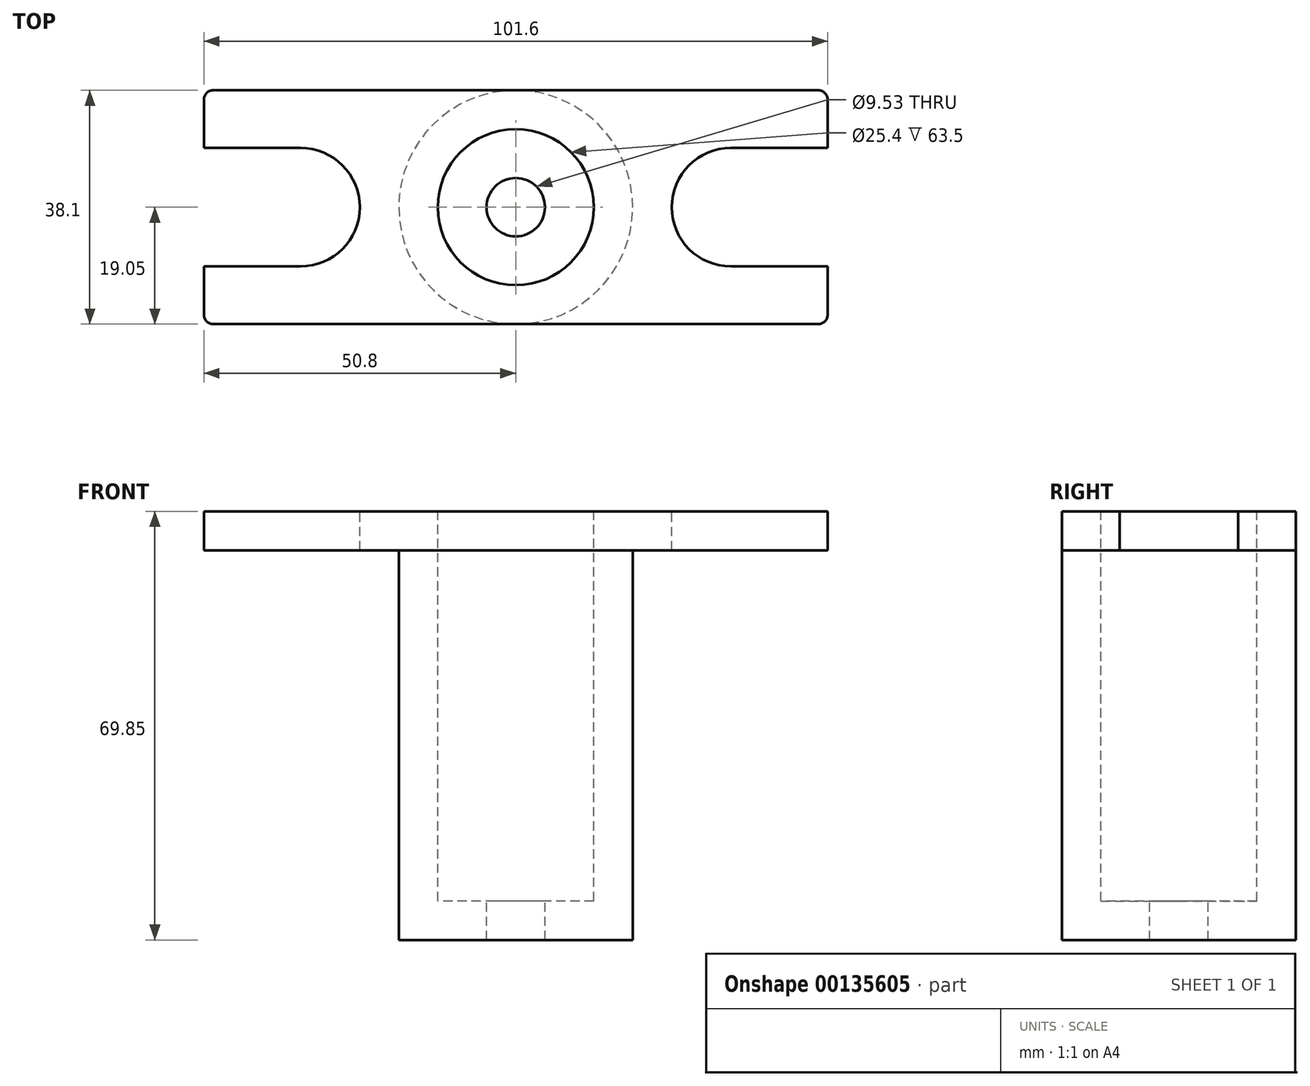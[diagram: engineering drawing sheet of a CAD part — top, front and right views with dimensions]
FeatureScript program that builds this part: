
annotation { "Feature Type Name" : "Feature", "Feature Type Description" : "" }
export const myFeature = defineFeature(function(context is Context, id is Id, definition is map)
    precondition{}
    {
        {
            var Q0;
            Q0=qCreatedBy(makeId("Front.planeOp"),FACE);
            var sketch = newSketch(context, id + "F0", { "sketchPlane" : qUnion([Q0])});
            skLineSegment(sketch, "E0", {"start": v(0, -26.8) * mm, "end": v(0, 86.68) * mm, "construction": true});
            skLineSegment(sketch, "E1", {"start": v(0, 69.85) * mm, "end": v(50.8, 69.85) * mm});
            skLineSegment(sketch, "E2", {"start": v(50.8, 69.85) * mm, "end": v(50.8, 63.5) * mm});
            skLineSegment(sketch, "E3", {"start": v(50.8, 63.5) * mm, "end": v(0, 63.5) * mm});
            skLineSegment(sketch, "E4", {"start": v(19.05, 63.5) * mm, "end": v(19.05, 0) * mm});
            skLineSegment(sketch, "E5", {"start": v(19.05, 0) * mm, "end": v(0, 0) * mm});
            skLineSegment(sketch, "E6", {"start": v(0, 0) * mm, "end": v(0, 69.85) * mm});
            skSolve(sketch);
        }
        {
            var Q0;
            Q0 = qSketchRegion(id + "F0", true);
            var Q1;
            Q1=sQuery(id+"F0.wireOp",EDGE,"E0");
            revolve(context, id + "F1", {"entities" : qUnion([Q0]), "axis" : qUnion([Q1]), "revolveType" : RevolveType.FULL});
        }
        {
            var Q0;
            Q0=makeQuery(id+"F1.opRevolve","SWEPT_FACE",FACE,{"disambiguationData":[OSD([sQuery(id+"F0.wireOp",EDGE,"E1")])]});
            var sketch = newSketch(context, id + "F2", { "sketchPlane" : qUnion([Q0])});
            skLineSegment(sketch, "E7.bottom", {"start": v(-50.8, 19.05) * mm, "end": v(50.8, 19.05) * mm});
            skLineSegment(sketch, "E7.top", {"start": v(-50.8, -19.05) * mm, "end": v(50.8, -19.05) * mm});
            skLineSegment(sketch, "E7.left", {"start": v(-50.8, 19.05) * mm, "end": v(-50.8, -19.05) * mm});
            skLineSegment(sketch, "E7.right", {"start": v(50.8, 19.05) * mm, "end": v(50.8, -19.05) * mm});
            skLineSegment(sketch, "E8", {"start": v(-73.34, 0) * mm, "end": v(77.6, 0) * mm, "construction": true});
            skLineSegment(sketch, "E9", {"start": v(0, -57.62) * mm, "end": v(0, 62.73) * mm, "construction": true});
            skSolve(sketch);
        }
        {
            var Q0;
            {var subQ0=sQuery(id+"F2.wireOp",EDGE,"E7.left");var subQ1=sQuery(id+"F2.wireOp",EDGE,"E7.bottom");var subQ2=makeQuery(id+"F2.imprint","INTERSECT",VERTEX,{"derivedFrom":[subQ1,subQ0]});Q0=makeQuery(id+"F2.imprint","IMPRINT",FACE,{"disambiguationData":[TD([[makeQuery(id+"F2.imprint","IMPRINT",EDGE,{"disambiguationData":[TD([[subQ2,-1.0]])],"derivedFrom":subQ1}),-1.0]])]});}
            var Q1;
            {var subQ0=sQuery(id+"F2.wireOp",EDGE,"E7.right");var subQ1=sQuery(id+"F2.wireOp",EDGE,"E7.bottom");var subQ2=makeQuery(id+"F2.imprint","INTERSECT",VERTEX,{"derivedFrom":[subQ1,subQ0]});Q1=makeQuery(id+"F2.imprint","IMPRINT",FACE,{"disambiguationData":[TD([[makeQuery(id+"F2.imprint","IMPRINT",EDGE,{"disambiguationData":[TD([[subQ2,1.0]])],"derivedFrom":subQ1}),-1.0]])]});}
            var Q2;
            {var subQ0=sQuery(id+"F2.wireOp",EDGE,"E7.left");var subQ1=sQuery(id+"F2.wireOp",EDGE,"E7.top");var subQ2=makeQuery(id+"F2.imprint","INTERSECT",VERTEX,{"derivedFrom":[subQ1,subQ0]});Q2=makeQuery(id+"F2.imprint","IMPRINT",FACE,{"disambiguationData":[TD([[makeQuery(id+"F2.imprint","IMPRINT",EDGE,{"disambiguationData":[TD([[subQ2,-1.0]])],"derivedFrom":subQ1}),1.0]])]});}
            var Q3;
            {var subQ0=sQuery(id+"F2.wireOp",EDGE,"E7.right");var subQ1=sQuery(id+"F2.wireOp",EDGE,"E7.top");var subQ2=makeQuery(id+"F2.imprint","INTERSECT",VERTEX,{"derivedFrom":[subQ1,subQ0]});Q3=makeQuery(id+"F2.imprint","IMPRINT",FACE,{"disambiguationData":[TD([[makeQuery(id+"F2.imprint","IMPRINT",EDGE,{"disambiguationData":[TD([[subQ2,1.0]])],"derivedFrom":subQ1}),1.0]])]});}
            var Q4;
            {var subQ0=sQuery(id+"F2.wireOp",EDGE,"E7.top");var subQ1=makeQuery(id+"F1.opRevolve","SWEPT_EDGE",EDGE,{"disambiguationData":[OSD([sQuery(id+"F0.wireOp",EDGE,"E1"),sQuery(id+"F0.wireOp",EDGE,"E2")])]});var subQ2=makeQuery(id+"F2.imprint","INTERSECT",VERTEX,{"disambiguationData":[OD(0.0)],"derivedFrom":[subQ1,subQ0]});Q4=makeQuery(id+"F2.imprint","IMPRINT",FACE,{"disambiguationData":[TD([[makeQuery(id+"F2.imprint","IMPRINT",EDGE,{"disambiguationData":[TD([[subQ2,-1.0]])],"derivedFrom":subQ0}),-1.0]])]});}
            var Q5;
            {var subQ0=sQuery(id+"F2.wireOp",EDGE,"E7.bottom");var subQ1=makeQuery(id+"F1.opRevolve","SWEPT_EDGE",EDGE,{"disambiguationData":[OSD([sQuery(id+"F0.wireOp",EDGE,"E1"),sQuery(id+"F0.wireOp",EDGE,"E2")])]});var subQ2=makeQuery(id+"F2.imprint","INTERSECT",VERTEX,{"disambiguationData":[OD(0.0)],"derivedFrom":[subQ1,subQ0]});Q5=makeQuery(id+"F2.imprint","IMPRINT",FACE,{"disambiguationData":[TD([[makeQuery(id+"F2.imprint","IMPRINT",EDGE,{"disambiguationData":[TD([[subQ2,-1.0]])],"derivedFrom":subQ0}),1.0]])]});}
            extrude(context, id + "F3", {"entities" : qUnion([Q0, Q1, Q2, Q3, Q4, Q5]), "operationType" : NewBodyOperationType.REMOVE, "endBound" : BoundingType.THROUGH_ALL, "oppositeDirection" : true, "depth" : 25.4 * mm});
        }
        {
            var Q0;
            Q0=makeQuery(id+"F1.opRevolve","SWEPT_FACE",FACE,{"disambiguationData":[OSD([sQuery(id+"F0.wireOp",EDGE,"E1")])]});
            var sketch = newSketch(context, id + "F4", { "sketchPlane" : qUnion([Q0])});
            skLineSegment(sketch, "E10.0.0", {"start": v(-47.1, 19.05) * mm, "end": v(-50.8, 19.05) * mm});
            skLineSegment(sketch, "E10.0.1", {"start": v(-50.8, 19.05) * mm, "end": v(-50.8, 0) * mm});
            skArc(sketch, "E10.0.2", {"start": v(-50.8, 0) * mm, "mid": v(-49.86, 9.7) * mm, "end": v(-47.1, 19.05) * mm});
            skLineSegment(sketch, "E11.0.0", {"start": v(-50.8, 0) * mm, "end": v(-50.8, -19.05) * mm});
            skLineSegment(sketch, "E11.0.1", {"start": v(-50.8, -19.05) * mm, "end": v(-47.1, -19.05) * mm});
            skArc(sketch, "E11.0.2", {"start": v(-47.1, -19.05) * mm, "mid": v(-49.86, -9.7) * mm, "end": v(-50.8, 0) * mm});
            skArc(sketch, "E12.0.0", {"start": v(50.8, 0) * mm, "mid": v(49.86, -9.7) * mm, "end": v(47.1, -19.05) * mm});
            skLineSegment(sketch, "E12.0.1", {"start": v(47.1, -19.05) * mm, "end": v(50.8, -19.05) * mm});
            skLineSegment(sketch, "E12.0.2", {"start": v(50.8, -19.05) * mm, "end": v(50.8, 0) * mm});
            skLineSegment(sketch, "E13.0.0", {"start": v(50.8, 19.05) * mm, "end": v(47.1, 19.05) * mm});
            skArc(sketch, "E13.0.1", {"start": v(47.1, 19.05) * mm, "mid": v(49.86, 9.7) * mm, "end": v(50.8, 0) * mm});
            skLineSegment(sketch, "E13.0.2", {"start": v(50.8, 0) * mm, "end": v(50.8, 19.05) * mm});
            skSolve(sketch);
        }
        {
            var Q0;
            Q0 = qSketchRegion(id + "F4", true);
            var Q1;
            Q1=makeQuery(id+"F3.boolean.opBoolean","SPLIT",FACE,{"disambiguationData":[OD(1.0)],"derivedFrom":makeQuery(id+"F1.opRevolve","SWEPT_FACE",FACE,{"disambiguationData":[OSD([sQuery(id+"F0.wireOp",EDGE,"E3")])]})});
            extrude(context, id + "F5", {"entities" : qUnion([Q0]), "operationType" : NewBodyOperationType.ADD, "endBound" : BoundingType.UP_TO_SURFACE, "oppositeDirection" : true, "endBoundEntityFace" : qUnion([Q1]), "depth" : 25.4 * mm});
        }
        {
            var Q0;
            {var subQ0=sQuery(id+"F2.wireOp",EDGE,"E7.bottom");var subQ1=makeQuery(id+"F1.opRevolve","SWEPT_EDGE",EDGE,{"disambiguationData":[OSD([sQuery(id+"F0.wireOp",EDGE,"E1"),sQuery(id+"F0.wireOp",EDGE,"E2")])]});var subQ4=makeQuery(id+"F2.imprint","INTERSECT",VERTEX,{"disambiguationData":[OD(0.0)],"derivedFrom":[subQ1,subQ0]});Q0=makeQuery(id+"F2.imprint","IMPRINT",FACE,{"disambiguationData":[TD([[makeQuery(id+"F2.imprint","IMPRINT",EDGE,{"disambiguationData":[TD([[subQ4,-1.0]])],"derivedFrom":subQ0}),-1.0]])]});}
            var sketch = newSketch(context, id + "F6", { "sketchPlane" : qUnion([Q0])});
            skLineSegment(sketch, "E14", {"start": v(-50.8, 9.65) * mm, "end": v(-35.05, 9.65) * mm});
            skLineSegment(sketch, "E15", {"start": v(-50.8, -9.65) * mm, "end": v(-35.05, -9.65) * mm});
            skLineSegment(sketch, "E16", {"start": v(50.8, -9.65) * mm, "end": v(35.05, -9.65) * mm});
            skLineSegment(sketch, "E17", {"start": v(50.8, 9.65) * mm, "end": v(35.05, 9.65) * mm});
            skArc(sketch, "E18", {"start": v(35.05, 9.65) * mm, "mid": v(25.4, 0) * mm, "end": v(35.05, -9.65) * mm});
            skArc(sketch, "E19", {"start": v(-35.05, -9.65) * mm, "mid": v(-25.4, 0) * mm, "end": v(-35.05, 9.65) * mm});
            skCircle(sketch, "E20", {"center": v(0, 0) * mm, "radius": 12.7 * mm, "construction": true});
            skLineSegment(sketch, "E21", {"start": v(-50.8, -9.65) * mm, "end": v(-50.8, 9.65) * mm});
            skLineSegment(sketch, "E22", {"start": v(50.8, -9.65) * mm, "end": v(50.8, 9.65) * mm});
            skSolve(sketch);
        }
        {
            var Q0;
            {var subQ0=sQuery(id+"F6.wireOp",EDGE,"E19");Q0=makeQuery(id+"F6.imprint","IMPRINT",FACE,{"disambiguationData":[TD([[makeQuery(id+"F6.imprint","IMPRINT",EDGE,{"derivedFrom":subQ0}),1.0]])]});}
            var Q1;
            {var subQ0=sQuery(id+"F6.wireOp",EDGE,"E21");var subQ1=sQuery(id+"F6.wireOp",EDGE,"E14");var subQ2=makeQuery(id+"F6.imprint","INTERSECT",VERTEX,{"derivedFrom":[subQ1,subQ0]});Q1=makeQuery(id+"F6.imprint","IMPRINT",FACE,{"disambiguationData":[TD([[makeQuery(id+"F6.imprint","IMPRINT",EDGE,{"disambiguationData":[TD([[subQ2,-1.0]])],"derivedFrom":subQ1}),-1.0]])]});}
            var Q2;
            {var subQ0=sQuery(id+"F6.wireOp",EDGE,"E21");var subQ1=sQuery(id+"F6.wireOp",EDGE,"E15");var subQ2=makeQuery(id+"F6.imprint","INTERSECT",VERTEX,{"derivedFrom":[subQ1,subQ0]});Q2=makeQuery(id+"F6.imprint","IMPRINT",FACE,{"disambiguationData":[TD([[makeQuery(id+"F6.imprint","IMPRINT",EDGE,{"disambiguationData":[TD([[subQ2,-1.0]])],"derivedFrom":subQ1}),1.0]])]});}
            var Q3;
            {var subQ0=sQuery(id+"F6.wireOp",EDGE,"E18");Q3=makeQuery(id+"F6.imprint","IMPRINT",FACE,{"disambiguationData":[TD([[makeQuery(id+"F6.imprint","IMPRINT",EDGE,{"derivedFrom":subQ0}),1.0]])]});}
            var Q4;
            {var subQ0=sQuery(id+"F6.wireOp",EDGE,"E22");var subQ1=sQuery(id+"F6.wireOp",EDGE,"E17");var subQ2=makeQuery(id+"F6.imprint","INTERSECT",VERTEX,{"derivedFrom":[subQ1,subQ0]});Q4=makeQuery(id+"F6.imprint","IMPRINT",FACE,{"disambiguationData":[TD([[makeQuery(id+"F6.imprint","IMPRINT",EDGE,{"disambiguationData":[TD([[subQ2,-1.0]])],"derivedFrom":subQ1}),1.0]])]});}
            var Q5;
            {var subQ0=sQuery(id+"F6.wireOp",EDGE,"E22");var subQ1=sQuery(id+"F6.wireOp",EDGE,"E16");var subQ2=makeQuery(id+"F6.imprint","INTERSECT",VERTEX,{"derivedFrom":[subQ1,subQ0]});Q5=makeQuery(id+"F6.imprint","IMPRINT",FACE,{"disambiguationData":[TD([[makeQuery(id+"F6.imprint","IMPRINT",EDGE,{"disambiguationData":[TD([[subQ2,-1.0]])],"derivedFrom":subQ1}),-1.0]])]});}
            extrude(context, id + "F7", {"entities" : qUnion([Q0, Q1, Q2, Q3, Q4, Q5]), "operationType" : NewBodyOperationType.REMOVE, "endBound" : BoundingType.THROUGH_ALL, "oppositeDirection" : true, "depth" : 25.4 * mm});
        }
        {
            var Q0;
            Q0=makeQuery(id+"F5.boolean.opBoolean","MERGE",FACE,{"derivedFrom":[makeQuery(id+"F1.opRevolve","SWEPT_FACE",FACE,{"disambiguationData":[OSD([sQuery(id+"F0.wireOp",EDGE,"E1")])]}),makeQuery(id+"F5.opExtrude","CAP_FACE",FACE,{"disambiguationData":[OSD([sQuery(id+"F4.wireOp",EDGE,"E10.0.0"),sQuery(id+"F4.wireOp",EDGE,"E10.0.1"),sQuery(id+"F4.wireOp",EDGE,"E10.0.2")])],"isStart":true}),makeQuery(id+"F5.opExtrude","CAP_FACE",FACE,{"disambiguationData":[OSD([sQuery(id+"F4.wireOp",EDGE,"E11.0.0"),sQuery(id+"F4.wireOp",EDGE,"E11.0.1"),sQuery(id+"F4.wireOp",EDGE,"E11.0.2")])],"isStart":true}),makeQuery(id+"F5.opExtrude","CAP_FACE",FACE,{"disambiguationData":[OSD([sQuery(id+"F4.wireOp",EDGE,"E12.0.0"),sQuery(id+"F4.wireOp",EDGE,"E12.0.1"),sQuery(id+"F4.wireOp",EDGE,"E12.0.2")])],"isStart":true}),makeQuery(id+"F5.opExtrude","CAP_FACE",FACE,{"disambiguationData":[OSD([sQuery(id+"F4.wireOp",EDGE,"E13.0.0"),sQuery(id+"F4.wireOp",EDGE,"E13.0.1"),sQuery(id+"F4.wireOp",EDGE,"E13.0.2")])],"isStart":true})]});
            var sketch = newSketch(context, id + "F8", { "sketchPlane" : qUnion([Q0])});
            skLineSegment(sketch, "E23", {"start": v(49.28, 19.05) * mm, "end": v(50.8, 19.05) * mm});
            skLineSegment(sketch, "E24", {"start": v(50.8, 19.05) * mm, "end": v(50.8, 17.53) * mm});
            skLineSegment(sketch, "E25", {"start": v(50.8, -19.05) * mm, "end": v(49.28, -19.05) * mm});
            skLineSegment(sketch, "E26", {"start": v(50.8, -19.05) * mm, "end": v(50.8, -17.53) * mm});
            skLineSegment(sketch, "E27", {"start": v(-50.8, -19.05) * mm, "end": v(-50.8, -17.53) * mm});
            skLineSegment(sketch, "E28", {"start": v(-50.8, -19.05) * mm, "end": v(-49.28, -19.05) * mm});
            skLineSegment(sketch, "E29", {"start": v(-50.8, 19.05) * mm, "end": v(-50.8, 17.53) * mm});
            skLineSegment(sketch, "E30", {"start": v(-50.8, 19.05) * mm, "end": v(-49.28, 19.05) * mm});
            skArc(sketch, "E31", {"start": v(-49.28, 19.05) * mm, "mid": v(-50.35, 18.6) * mm, "end": v(-50.8, 17.53) * mm});
            skArc(sketch, "E32", {"start": v(50.8, 17.53) * mm, "mid": v(50.35, 18.6) * mm, "end": v(49.28, 19.05) * mm});
            skArc(sketch, "E33", {"start": v(49.28, -19.05) * mm, "mid": v(50.35, -18.6) * mm, "end": v(50.8, -17.53) * mm});
            skArc(sketch, "E34", {"start": v(-50.8, -17.53) * mm, "mid": v(-50.35, -18.6) * mm, "end": v(-49.28, -19.05) * mm});
            skSolve(sketch);
        }
        {
            var Q0;
            Q0 = qSketchRegion(id + "F8", true);
            extrude(context, id + "F9", {"entities" : qUnion([Q0]), "operationType" : NewBodyOperationType.REMOVE, "endBound" : BoundingType.THROUGH_ALL, "oppositeDirection" : true, "depth" : 25.4 * mm});
        }
        {
            var Q0;
            Q0=qCreatedBy(makeId("Front.planeOp"),FACE);
            var sketch = newSketch(context, id + "F10", { "sketchPlane" : qUnion([Q0])});
            skLineSegment(sketch, "E35", {"start": v(0, -43.81) * mm, "end": v(0, 118.66) * mm, "construction": true});
            skLineSegment(sketch, "E36.bottom", {"start": v(0, 69.85) * mm, "end": v(12.7, 69.85) * mm});
            skLineSegment(sketch, "E36.top", {"start": v(0, 6.35) * mm, "end": v(12.7, 6.35) * mm});
            skLineSegment(sketch, "E36.left", {"start": v(0, 69.85) * mm, "end": v(0, 6.35) * mm});
            skLineSegment(sketch, "E36.right", {"start": v(12.7, 69.85) * mm, "end": v(12.7, 6.35) * mm});
            skLineSegment(sketch, "E37.bottom", {"start": v(0, 6.35) * mm, "end": v(4.76, 6.35) * mm});
            skLineSegment(sketch, "E37.top", {"start": v(0, 0) * mm, "end": v(4.76, 0) * mm});
            skLineSegment(sketch, "E37.left", {"start": v(0, 6.35) * mm, "end": v(0, 0) * mm});
            skLineSegment(sketch, "E37.right", {"start": v(4.76, 6.35) * mm, "end": v(4.76, 0) * mm});
            skSolve(sketch);
        }
        {
            var Q0;
            Q0 = qSketchRegion(id + "F10", true);
            var Q1;
            Q1=sQuery(id+"F10.wireOp",EDGE,"E35");
            revolve(context, id + "F11", {"operationType" : NewBodyOperationType.REMOVE, "entities" : qUnion([Q0]), "axis" : qUnion([Q1]), "revolveType" : RevolveType.FULL, "oppositeDirection" : true});
        }
    });
